# Revit family: AA01900000
name_source: partatom
category: Apparecchi idraulici
units: mm (PartAtom-declared; Revit-internal decimal feet)

## family parameters
Basato su piano di lavoro = No
Condiviso = No
Numero OmniClass = 23.45.00.00
Punto di calcolo locali = No
Quota connettore circolare = Usa diametro
Sempre verticale = Sì
Taglio con vuoti quando caricato = No
Tipo di parte = Normale
Titolo OmniClass = Sanitary, Laundry, and Cleaning Equipment

## types (1)
- AA01900000
    Commenti sul tipo = Realizzato in ottemperanza ai requisiti gestionali della norma EN ISO 9001. Collaudato al 100% secondo la normativa EN 12266-1.
    Descrizione = Utilizzato nei più svariati settori dell'impiantistica: impianti di riscaldamento, condizionamento, idrici, igienico-sanitari, reti di distribuzione oli, benzine, vapore saturo e in generale con ogni fluido non corrosivo
    Materiale = Prodotto in lega di bronzo conforme alla norma EN 1982-CC491K
    Modello = Cim 72FPN10
    Pressione nominale = PN 16 (DN 15 ÷ 100); PN 10 (DN 125 e 150)
    Produttore = CIMBERIO SPA
    Prospetto di default = 0 mm  [stored 0 ft]
    Temperatura di esercizio = -10 ÷ 170°C (DN 15 ÷ 100); -10 ÷ 150°C (DN 125 e 150)
    URL = https://web.cimberio.it

note: [stored X ft] marks values corroborated as IEEE doubles in the binary element streams (Revit-internal decimal feet)
